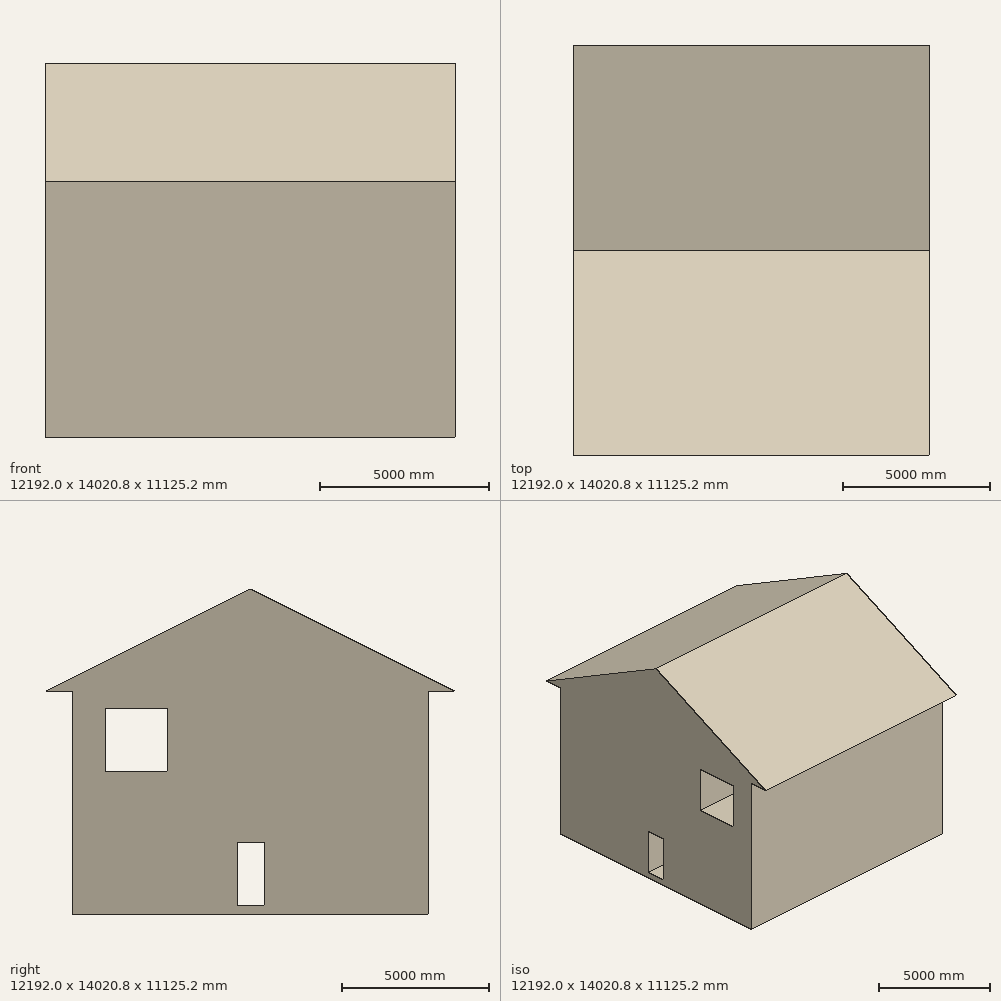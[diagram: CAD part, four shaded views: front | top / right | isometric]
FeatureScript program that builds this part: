
annotation { "Feature Type Name" : "Feature", "Feature Type Description" : "" }
export const myFeature = defineFeature(function(context is Context, id is Id, definition is map)
    precondition{}
    {
        {
            var Q0;
            Q0=qCreatedBy(makeId("Right.planeOp"),FACE);
            var sketch = newSketch(context, id + "F0", { "sketchPlane" : qUnion([Q0])});
            skLineSegment(sketch, "E0", {"start": v(-6096, 0) * mm, "end": v(0, 3048) * mm});
            skLineSegment(sketch, "E1", {"start": v(6096, 0) * mm, "end": v(0, 3048) * mm});
            skLineSegment(sketch, "E2", {"start": v(-6096, 0) * mm, "end": v(-6096, -7315.2) * mm});
            skLineSegment(sketch, "E3", {"start": v(-6096, -7315.2) * mm, "end": v(6096, -7315.2) * mm});
            skLineSegment(sketch, "E4", {"start": v(6096, 0) * mm, "end": v(6096, -7315.2) * mm});
            skLineSegment(sketch, "E5", {"start": v(-6096, -7315.2) * mm, "end": v(-6096, -7620) * mm});
            skLineSegment(sketch, "E6", {"start": v(-6096, -7620) * mm, "end": v(6096, -7620) * mm});
            skLineSegment(sketch, "E7", {"start": v(6096, -7315.2) * mm, "end": v(6096, -7620) * mm});
            skLineSegment(sketch, "E8", {"start": v(0, 0) * mm, "end": v(-6096, 0) * mm});
            skLineSegment(sketch, "E9", {"start": v(0, 0) * mm, "end": v(6096, 0) * mm});
            skLineSegment(sketch, "E10", {"start": v(-441.1, -5181.6) * mm, "end": v(473.3, -5181.6) * mm});
            skLineSegment(sketch, "E11", {"start": v(-441.1, -5181.6) * mm, "end": v(-441.1, -7315.2) * mm});
            skLineSegment(sketch, "E12", {"start": v(473.3, -5181.6) * mm, "end": v(473.3, -7315.2) * mm});
            skLineSegment(sketch, "E13", {"start": v(-6096, 0) * mm, "end": v(-7010.4, 0) * mm});
            skLineSegment(sketch, "E14", {"start": v(0, 3048) * mm, "end": v(0, 3505.2) * mm});
            skLineSegment(sketch, "E15", {"start": v(6096, 0) * mm, "end": v(7010.4, 0) * mm});
            skLineSegment(sketch, "E16", {"start": v(7010.4, 0) * mm, "end": v(0, 3505.2) * mm});
            skLineSegment(sketch, "E17", {"start": v(-7010.4, 0) * mm, "end": v(0, 3505.2) * mm});
            skLineSegment(sketch, "E18.bottom", {"start": v(-4970.04, -594.56) * mm, "end": v(-2836.44, -594.56) * mm});
            skLineSegment(sketch, "E18.top", {"start": v(-4970.04, -2728.16) * mm, "end": v(-2836.44, -2728.16) * mm});
            skLineSegment(sketch, "E18.left", {"start": v(-4970.04, -594.56) * mm, "end": v(-4970.04, -2728.16) * mm});
            skLineSegment(sketch, "E18.right", {"start": v(-2836.44, -594.56) * mm, "end": v(-2836.44, -2728.16) * mm});
            skLineSegment(sketch, "E19.bottom", {"start": v(-4605.09, -2496.55) * mm, "end": v(-3385.89, -2496.55) * mm});
            skLineSegment(sketch, "E19.top", {"start": v(-4605.09, -972.55) * mm, "end": v(-3385.89, -972.55) * mm});
            skLineSegment(sketch, "E19.left", {"start": v(-4605.09, -2496.55) * mm, "end": v(-4605.09, -972.55) * mm});
            skLineSegment(sketch, "E19.right", {"start": v(-3385.89, -2496.55) * mm, "end": v(-3385.89, -972.55) * mm});
            skSolve(sketch);
        }
        {
            var Q0;
            Q0=makeQuery(id+"F0.imprint","IMPRINT",FACE,{"disambiguationData":[TD([[makeQuery(id+"F0.imprint","IMPRINT",EDGE,{"derivedFrom":sQuery(id+"F0.wireOp",EDGE,"E0")}),-1.0]])]});
            var Q1;
            Q1=makeQuery(id+"F0.imprint","IMPRINT",FACE,{"disambiguationData":[TD([[makeQuery(id+"F0.imprint","IMPRINT",EDGE,{"derivedFrom":sQuery(id+"F0.wireOp",EDGE,"E1")}),-1.0]])]});
            var Q2;
            {var subQ1=sQuery(id+"F0.wireOp",EDGE,"E2");Q2=makeQuery(id+"F0.imprint","IMPRINT",FACE,{"disambiguationData":[TD([[makeQuery(id+"F0.imprint","IMPRINT",EDGE,{"derivedFrom":subQ1}),1.0]])]});}
            var Q3;
            Q3=makeQuery(id+"F0.imprint","IMPRINT",FACE,{"disambiguationData":[TD([[makeQuery(id+"F0.imprint","IMPRINT",EDGE,{"derivedFrom":sQuery(id+"F0.wireOp",EDGE,"E0")}),1.0]])]});
            var Q4;
            {var subQ0=sQuery(id+"F0.wireOp",EDGE,"E5");Q4=makeQuery(id+"F0.imprint","IMPRINT",FACE,{"disambiguationData":[TD([[makeQuery(id+"F0.imprint","IMPRINT",EDGE,{"derivedFrom":subQ0}),1.0]])]});}
            extrude(context, id + "F1", {"entities" : qUnion([Q0, Q1, Q2, Q3, Q4]), "depth" : 12192 * mm, "offsetDistance" : 30.48 * mm});
        }
    });
